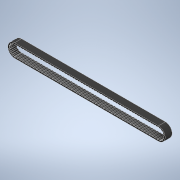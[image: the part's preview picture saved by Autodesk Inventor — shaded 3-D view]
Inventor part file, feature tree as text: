
AUTODESK INVENTOR PART (.ipt)
format: ipt  version: 2021 (Build 250183000, 183)  size: 981,504 bytes
history: native  units: in
note: dims shown in document units (in); Inventor stores cm internally (conversion verified against a paired STEP export)
features: other x120, sketch x3, pattern_linear x2, extrude x2, fillet x1
ambient origin geometry x8: Origin, YZ Plane, XZ Plane, XY Plane, X Axis, Y Axis, Z Axis, Center Point
bodies: Solid1 (feature_tree)
feature tree (128):
  sketch  "Sketch1"  dims[d0=0.6693in]
  other  "Work Point1"
  pattern_linear  "Rectangular Pattern1"  Count1=120 Spacing1=0.3937in
  extrude  "Extrusion1"  Depth=0.4134in
  fillet  "Fillet1"  Radius=0.0394in
  pattern_linear  "Rectangular Pattern2"  Spacing1=0.0394in  [1 undecoded]
  extrude  "Extrusion2"  Depth=0.4134in TaperAngle=0.0deg
  other  "Work Point2"
  other  "Work Point3"
  other  "Work Point4"
  other  "Work Point5"
  other  "Work Point6"
  other  "Work Point7"
  other  "Work Point8"
  other  "Work Point9"
  other  "Work Point10"
  other  "Work Point11"
  other  "Work Point12"
  other  "Work Point13"
  other  "Work Point14"
  other  "Work Point15"
  other  "Work Point16"
  other  "Work Point17"
  other  "Work Point18"
  other  "Work Point19"
  other  "Work Point20"
  other  "Work Point21"
  other  "Work Point22"
  other  "Work Point23"
  other  "Work Point24"
  other  "Work Point25"
  other  "Work Point26"
  other  "Work Point27"
  other  "Work Point28"
  other  "Work Point29"
  other  "Work Point30"
  other  "Work Point31"
  other  "Work Point32"
  other  "Work Point33"
  other  "Work Point34"
  other  "Work Point35"
  other  "Work Point36"
  other  "Work Point37"
  other  "Work Point38"
  other  "Work Point39"
  other  "Work Point40"
  other  "Work Point41"
  other  "Work Point42"
  other  "Work Point43"
  other  "Work Point44"
  other  "Work Point45"
  other  "Work Point46"
  other  "Work Point47"
  other  "Work Point48"
  other  "Work Point49"
  other  "Work Point50"
  other  "Work Point51"
  other  "Work Point52"
  other  "Work Point53"
  other  "Work Point54"
  other  "Work Point55"
  other  "Work Point56"
  other  "Work Point57"
  other  "Work Point58"
  other  "Work Point59"
  other  "Work Point60"
  other  "Work Point61"
  other  "Work Point62"
  other  "Work Point63"
  other  "Work Point64"
  other  "Work Point65"
  other  "Work Point66"
  other  "Work Point67"
  other  "Work Point68"
  other  "Work Point69"
  other  "Work Point70"
  other  "Work Point71"
  other  "Work Point72"
  other  "Work Point73"
  other  "Work Point74"
  other  "Work Point75"
  other  "Work Point76"
  other  "Work Point77"
  other  "Work Point78"
  other  "Work Point79"
  other  "Work Point80"
  other  "Work Point81"
  other  "Work Point82"
  other  "Work Point83"
  other  "Work Point84"
  other  "Work Point85"
  other  "Work Point86"
  other  "Work Point87"
  other  "Work Point88"
  other  "Work Point89"
  other  "Work Point90"
  other  "Work Point91"
  other  "Work Point92"
  other  "Work Point93"
  other  "Work Point94"
  other  "Work Point95"
  other  "Work Point96"
  other  "Work Point97"
  other  "Work Point98"
  other  "Work Point99"
  other  "Work Point100"
  other  "Work Point101"
  other  "Work Point102"
  other  "Work Point103"
  other  "Work Point104"
  other  "Work Point105"
  other  "Work Point106"
  other  "Work Point107"
  other  "Work Point108"
  other  "Work Point109"
  other  "Work Point110"
  other  "Work Point111"
  other  "Work Point112"
  other  "Work Point113"
  other  "Work Point114"
  other  "Work Point115"
  other  "Work Point116"
  other  "Work Point117"
  other  "Work Point118"
  other  "Work Point119"
  other  "Work Point120"
  sketch  "Sketch2"  dims[d1=8.4646in d2=47.2441in d4=0.3937in]
  sketch  "Sketch3"  dims[d5=0.1181in d6=0.0394in d7=0.0394in d8=0.0394in d9=0.4134in d10=0.0in d11=0.0197in d12=47.2441in d14=0.0591in d15=0.4134in d16=0.0in]
note: 1 required parameter value undecoded (feature->parameter linkage not recoverable at this tier; creation-order binding heuristic only, values carry confidence <= 0.55)
